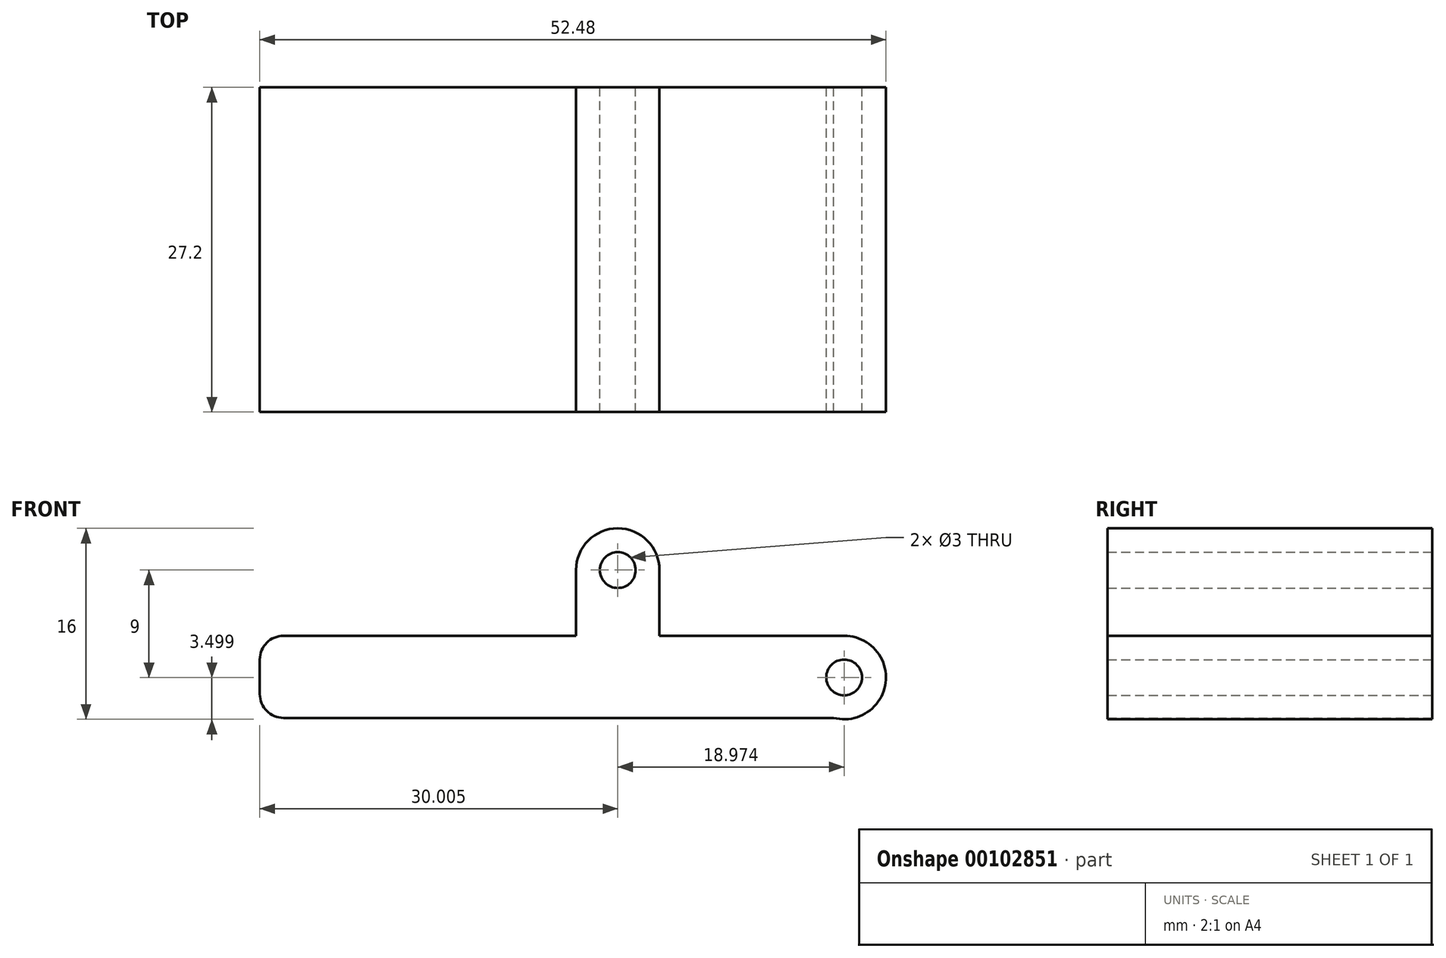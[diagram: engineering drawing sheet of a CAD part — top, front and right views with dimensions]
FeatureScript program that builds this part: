
annotation { "Feature Type Name" : "Feature", "Feature Type Description" : "" }
export const myFeature = defineFeature(function(context is Context, id is Id, definition is map)
    precondition{}
    {
        {
            var Q0;
            Q0=qCreatedBy(makeId("Front.planeOp"),FACE);
            var sketch = newSketch(context, id + "F0", { "sketchPlane" : qUnion([Q0])});
            skCircle(sketch, "E0", {"center": v(-41.2, 7.77) * mm, "radius": 3.5 * mm});
            skCircle(sketch, "E1", {"center": v(-22.23, 16.77) * mm, "radius": 3.5 * mm});
            skLineSegment(sketch, "E2.bottom", {"start": v(-22.23, 13.27) * mm, "end": v(-69.2, 13.27) * mm});
            skLineSegment(sketch, "E2.top", {"start": v(-22.23, 20.16) * mm, "end": v(-69.2, 20.16) * mm});
            skLineSegment(sketch, "E2.left", {"start": v(-22.23, 13.27) * mm, "end": v(-22.23, 20.16) * mm});
            skLineSegment(sketch, "E2.right", {"start": v(-71.2, 15.27) * mm, "end": v(-71.2, 18.16) * mm});
            skLineSegment(sketch, "E3", {"start": v(-44.7, 7.77) * mm, "end": v(-44.7, 13.27) * mm});
            skLineSegment(sketch, "E4", {"start": v(-37.7, 7.77) * mm, "end": v(-37.7, 13.27) * mm});
            skPoint(sketch, "E5.visualSharp", {"position": v(-71.2, 20.16) * mm});
            skArc(sketch, "E5.filletArc", {"start": v(-69.2, 20.16) * mm, "mid": v(-70.62, 19.58) * mm, "end": v(-71.2, 18.16) * mm});
            skPoint(sketch, "E6.visualSharp", {"position": v(-71.2, 13.27) * mm});
            skArc(sketch, "E6.filletArc", {"start": v(-71.2, 15.27) * mm, "mid": v(-70.62, 13.86) * mm, "end": v(-69.2, 13.27) * mm});
            skSolve(sketch);
        }
        {
            var Q0;
            Q0 = qSketchRegion(id + "F0", true);
            extrude(context, id + "F1", {"entities" : qUnion([Q0]), "oppositeDirection" : true, "depth" : 27.2 * mm});
        }
        {
            var Q0;
            Q0=sQuery(id+"F0.wireOp",VERTEX,"E0.center");
            var Q1;
            Q1=makeQuery(id+"F1.opExtrude","SWEPT_BODY",BODY,{"disambiguationData":[OSD([sQuery(id+"F0.wireOp",EDGE,"E0"),sQuery(id+"F0.wireOp",EDGE,"E1"),sQuery(id+"F0.wireOp",EDGE,"E2.bottom"),sQuery(id+"F0.wireOp",EDGE,"E2.top"),sQuery(id+"F0.wireOp",EDGE,"E2.right"),sQuery(id+"F0.wireOp",EDGE,"E3"),sQuery(id+"F0.wireOp",EDGE,"E4"),sQuery(id+"F0.wireOp",EDGE,"E5.filletArc"),sQuery(id+"F0.wireOp",EDGE,"E6.filletArc")])]});
            hole(context, id + "F2", {"style" : HoleStyle.SIMPLE, "endStyle" : HoleEndStyle.THROUGH, "holeDiameter" : 3 * mm, "locations" : qUnion([Q0]), "scope" : qUnion([Q1]), "isTappedThrough" : true});
        }
        {
            var Q0;
            Q0=sQuery(id+"F0.wireOp",VERTEX,"E1.center");
            var Q1;
            Q1=makeQuery(id+"F1.opExtrude","SWEPT_BODY",BODY,{"disambiguationData":[OSD([sQuery(id+"F0.wireOp",EDGE,"E0"),sQuery(id+"F0.wireOp",EDGE,"E1"),sQuery(id+"F0.wireOp",EDGE,"E2.bottom"),sQuery(id+"F0.wireOp",EDGE,"E2.top"),sQuery(id+"F0.wireOp",EDGE,"E2.right"),sQuery(id+"F0.wireOp",EDGE,"E3"),sQuery(id+"F0.wireOp",EDGE,"E4"),sQuery(id+"F0.wireOp",EDGE,"E5.filletArc"),sQuery(id+"F0.wireOp",EDGE,"E6.filletArc")])]});
            hole(context, id + "F3", {"style" : HoleStyle.SIMPLE, "endStyle" : HoleEndStyle.THROUGH, "holeDiameter" : 3 * mm, "locations" : qUnion([Q0]), "scope" : qUnion([Q1]), "isTappedThrough" : true});
        }
        {
            var Q0;
            Q0=makeQuery(id+"F1.opExtrude","SWEPT_BODY",BODY,{"disambiguationData":[OSD([sQuery(id+"F0.wireOp",EDGE,"E0"),sQuery(id+"F0.wireOp",EDGE,"E1"),sQuery(id+"F0.wireOp",EDGE,"E2.bottom"),sQuery(id+"F0.wireOp",EDGE,"E2.top"),sQuery(id+"F0.wireOp",EDGE,"E2.right"),sQuery(id+"F0.wireOp",EDGE,"E3"),sQuery(id+"F0.wireOp",EDGE,"E4"),sQuery(id+"F0.wireOp",EDGE,"E5.filletArc"),sQuery(id+"F0.wireOp",EDGE,"E6.filletArc")])]});
            var Q1;
            Q1=makeQuery(id+"F1.opExtrude","CAP_EDGE",EDGE,{"disambiguationData":[OSD([sQuery(id+"F0.wireOp",EDGE,"E2.top")])],"isStart":true});
            transform(context, id + "F4", {"entities" : qUnion([Q0]), "transformType" : TransformType.ROTATION, "transformAxis" : qUnion([Q1]), "angle" : 180 * degree, "makeCopy" : false});
        }
    });
